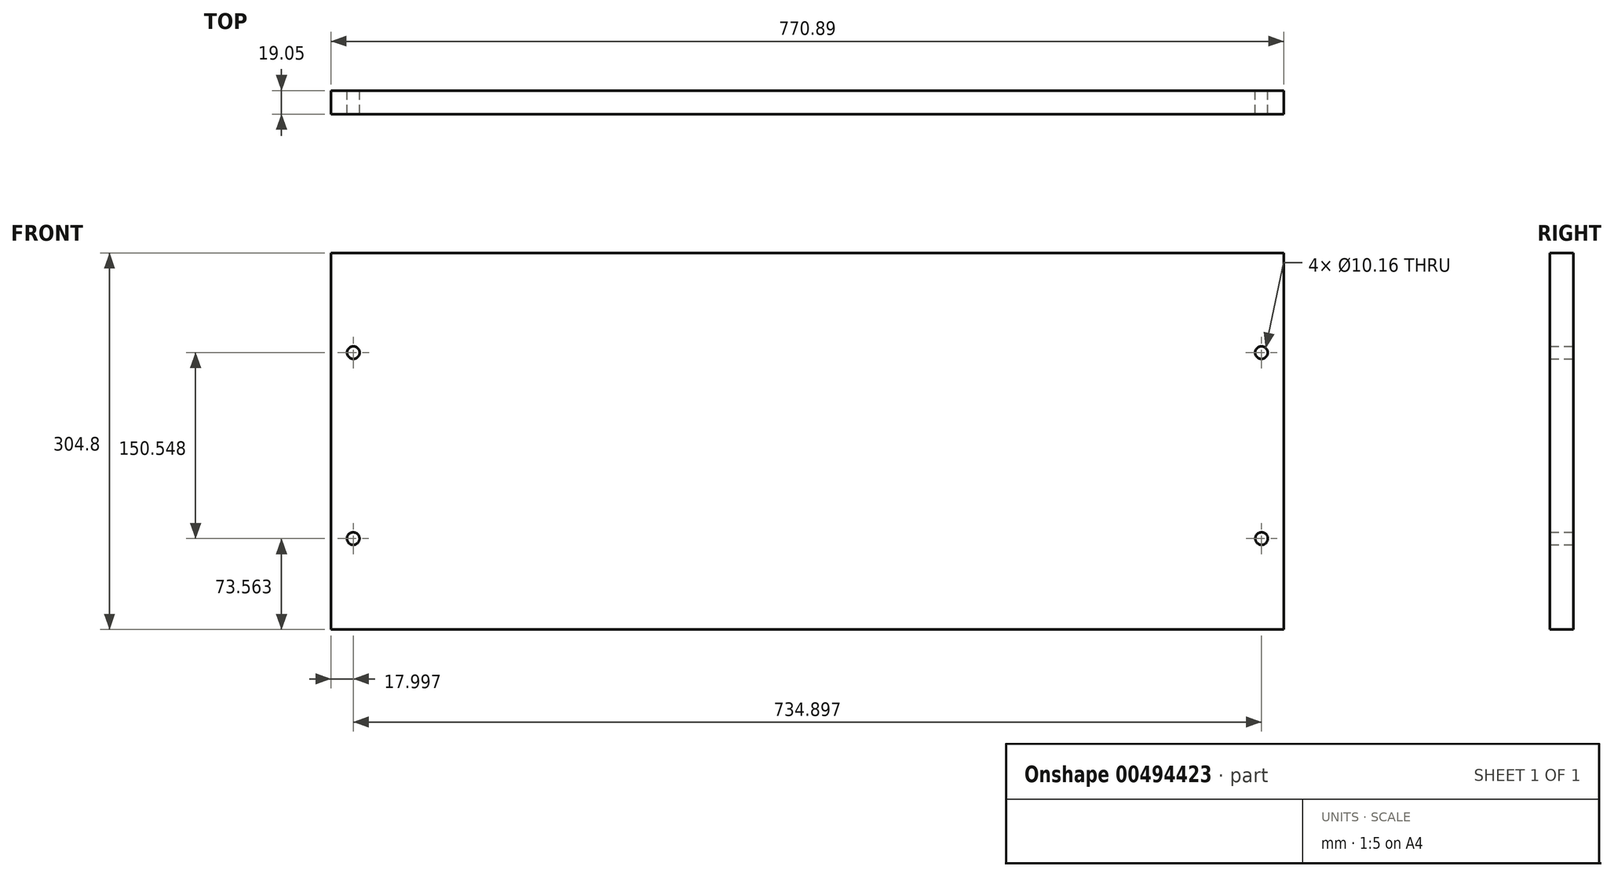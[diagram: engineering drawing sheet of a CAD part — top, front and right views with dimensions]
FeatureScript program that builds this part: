
annotation { "Feature Type Name" : "Feature", "Feature Type Description" : "" }
export const myFeature = defineFeature(function(context is Context, id is Id, definition is map)
    precondition{}
    {
        {
            var Q0;
            Q0=qCreatedBy(makeId("Front.planeOp"),FACE);
            var sketch = newSketch(context, id + "F0", { "sketchPlane" : qUnion([Q0])});
            skLineSegment(sketch, "E0", {"start": v(0, 0) * mm, "end": v(770.9, 0) * mm});
            skLineSegment(sketch, "E1", {"start": v(0, 0) * mm, "end": v(0, 304.8) * mm});
            skLineSegment(sketch, "E2", {"start": v(0, 304.8) * mm, "end": v(770.9, 304.8) * mm});
            skLineSegment(sketch, "E3", {"start": v(770.9, 304.8) * mm, "end": v(770.9, 0) * mm});
            skCircle(sketch, "E4", {"center": v(18, 73.56) * mm, "radius": 5.08 * mm});
            skCircle(sketch, "E5", {"center": v(18.08, 224.11) * mm, "radius": 5.08 * mm});
            skLineSegment(sketch, "E6", {"start": v(385.45, 304.8) * mm, "end": v(385.45, -64.5) * mm, "construction": true});
            skCircle(sketch, "E7.MirrorC", {"center": v(752.81, 224.11) * mm, "radius": 5.08 * mm});
            skCircle(sketch, "E8.MirrorC", {"center": v(752.9, 73.56) * mm, "radius": 5.08 * mm});
            skSolve(sketch);
        }
        {
            var Q0;
            Q0=makeQuery(id+"F0.imprint","IMPRINT",FACE,{"disambiguationData":[TD([[makeQuery(id+"F0.imprint","IMPRINT",EDGE,{"derivedFrom":sQuery(id+"F0.wireOp",EDGE,"E0")}),1.0]])]});
            extrude(context, id + "F1", {"entities" : qUnion([Q0]), "depth" : 19.05 * mm});
        }
    });
